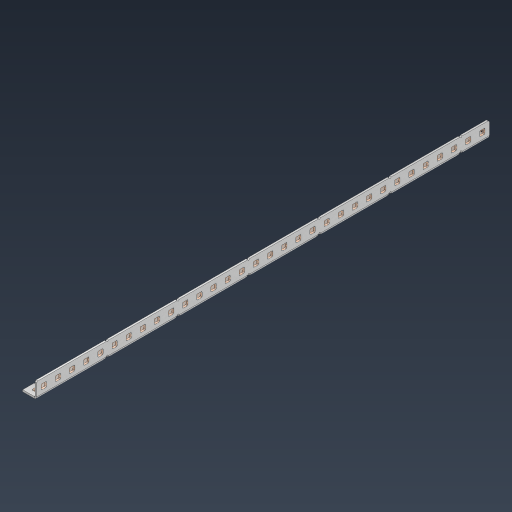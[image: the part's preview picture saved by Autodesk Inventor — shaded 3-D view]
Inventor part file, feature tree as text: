
AUTODESK INVENTOR PART (.ipt)
format: ipt  version: 2024.3 (Build 283343000, 343)  size: 1,180,160 bytes
history: native  units: in
note: dims shown in document units (in); Inventor stores cm internally (conversion verified against a paired STEP export)
features: other x103, extrude x94, sheet_metal_op x11, pattern_linear x2, mirror x1, chamfer x1, sketch x1
ambient origin geometry x8: Origin, YZ Plane, XZ Plane, XY Plane, X Axis, Y Axis, Z Axis, Center Point
bodies: Solid1 (feature_tree), Body (feature_tree)
feature tree (213):
  sheet_metal_op  "Flanges"
  other  "Flange Pattern Plane"
  other  "Flange Pattern Sketch"
  sheet_metal_op  "Flange Pattern"
  sheet_metal_op  "Body Pattern"
  pattern_linear  "Center Pattern"  Spacing1=16.0in  [1 undecoded]
  other  "Arc Length"
  mirror  "Notch Mirror"
  pattern_linear  "Notch Pattern"  Spacing1=0.0625in  [1 undecoded]
  chamfer  "End Chamfer"
  extrude  "Half Cut"  Depth=0.0625in
  other  "Plate1"
  sketch  "Sketch2"  dims[d0=1.0in d1=16.0in d2=0.0625in d3=0.0625in d4=0.0312in d5=0.125in d6=0.0625in d7=0.5in d8=90.0deg d9=0.0312in d10=0.25in d11=0.0625in d12=0.0625in d16=0.182in d17=0.02in d18=0.0625in d19=0.0in d20=0.25in d21=0.25in d38=12.5984in d40=0.5in d41=0.3937in d43=1.0in d46=0.172in d47=1.0in d48=0.0in d49=0.182in d50=0.02in d51=0.25in d52=0.25in d53=0.0625in d54=0.0in d55=0.172in d56=1.0in d57=0.0in d58=0.25in d60=12.5984in d62=0.5in d63=0.3937in d65=0.5in d85=0.1473in d86=0.1782in d88=0.04in d89=0.0625in d90=0.0in d91=0.04in d92=0.0491in d95=2.5in d96=0.04in d97=0.25in d98=45.0deg d99=0.25in d100=0.5in d101=0.0in d102=2.497in d106=0.182in d107=0.02in d108=0.5in d109=0.5in d110=0.0625in d111=0.0in d112=0.172in d113=0.5in d114=0.0in d117=0.5in d118=0.5in d119=0.5in]
  other  "Plate2"
  sheet_metal_op  "Bend1"
  sheet_metal_op  "Corner1"
  other  "Srf1"
  other  "Srf2"
  other  "Srf91"
  sheet_metal_op  "Body Pattern Sketch"
  other  "Srf92"
  other  "Srf786"
  other  "Srf823"
  other  "Srf824"
  other  "Srf825"
  other  "Srf826"
  other  "Srf827"
  other  "Srf828"
  other  "Srf829"
  other  "Srf856"
  other  "Srf857"
  other  "Srf858"
  other  "Srf859"
  other  "Srf860"
  other  "Srf861"
  other  "Srf862"
  other  "Srf889"
  other  "Srf890"
  other  "Srf891"
  other  "Srf892"
  other  "Srf893"
  other  "Srf894"
  other  "Srf895"
  other  "Srf896"
  other  "Srf922"
  other  "Srf923"
  other  "Srf924"
  other  "Srf925"
  other  "Srf926"
  other  "Srf959"
  other  "Srf960"
  other  "Srf961"
  other  "Srf962"
  other  "Srf963"
  other  "Srf996"
  other  "Srf997"
  other  "Srf998"
  other  "Srf999"
  other  "Srf1000"
  other  "Srf1143"
  other  "Srf1144"
  other  "Srf1145"
  other  "Srf1146"
  other  "Srf1147"
  other  "Srf1148"
  other  "Srf1149"
  other  "Srf1150"
  other  "Srf1151"
  other  "Srf1152"
  other  "Srf1153"
  other  "Srf1154"
  other  "Srf1155"
  other  "Srf1156"
  other  "Srf1157"
  other  "Srf1158"
  other  "Srf1159"
  other  "Srf1160"
  other  "Srf1199"
  other  "Srf1200"
  other  "Srf1201"
  other  "Srf1202"
  other  "Srf1203"
  other  "Srf1204"
  other  "Srf1205"
  other  "Srf1206"
  other  "Srf1207"
  other  "Srf1208"
  other  "Srf1209"
  other  "Srf1210"
  other  "Srf1211"
  other  "Srf1212"
  other  "Srf1213"
  other  "Srf1214"
  other  "Srf1215"
  other  "Srf1216"
  other  "Srf1255"
  other  "Srf1256"
  other  "Srf1257"
  other  "Srf1258"
  other  "Srf1259"
  other  "Srf1260"
  other  "Srf1261"
  other  "Srf1262"
  other  "Srf1263"
  other  "Srf1264"
  other  "Srf1265"
  other  "Srf1266"
  other  "Srf1267"
  other  "Srf1268"
  other  "Srf1269"
  other  "Srf1270"
  other  "Srf1271"
  other  "Srf1272"
  sheet_metal_op  "Flange Stamp"
  sheet_metal_op  "Flange Circle"
  sheet_metal_op  "Body Stamp"
  sheet_metal_op  "Body Circle"
  other  "Center Stamp"
  other  "Center Circle"
  sheet_metal_op  "Notch"
  extrude  "ExtrusionSrf2"  Depth=0.0312in
  extrude  "ExtrusionSrf92"  Depth=0.5in
  extrude  "ExtrusionSrf823"  Depth=0.0625in
  extrude  "ExtrusionSrf824"  Depth=0.5in TaperAngle=90.0deg
  extrude  "ExtrusionSrf825"  Depth=0.25in
  extrude  "ExtrusionSrf826"  Depth=0.0625in
  extrude  "ExtrusionSrf827"  Depth=0.0625in
  extrude  "ExtrusionSrf828"  Depth=0.182in
  extrude  "ExtrusionSrf829"  Depth=0.02in
  extrude  "ExtrusionSrf856"  Depth=0.0625in
  extrude  "ExtrusionSrf857"  TaperAngle=0.0deg  [1 undecoded]
  extrude  "ExtrusionSrf858"  Depth=0.25in
  extrude  "ExtrusionSrf859"  Depth=0.25in
  extrude  "ExtrusionSrf860"  Depth=0.5in
  extrude  "ExtrusionSrf861"  Depth=0.5in
  extrude  "ExtrusionSrf862"  Depth=1.0in TaperAngle=0.0deg
  extrude  "ExtrusionSrf889"  Depth=0.182in
  extrude  "ExtrusionSrf890"  Depth=0.02in
  extrude  "ExtrusionSrf891"  Depth=0.25in
  extrude  "ExtrusionSrf892"  Depth=0.25in
  extrude  "ExtrusionSrf893"  Depth=0.0625in
  extrude  "ExtrusionSrf894"  TaperAngle=0.0deg  [1 undecoded]
  extrude  "ExtrusionSrf895"  Depth=0.5in
  extrude  "ExtrusionSrf896"  Depth=1.0in TaperAngle=0.0deg
  extrude  "ExtrusionSrf922"  Depth=0.25in
  extrude  "ExtrusionSrf923"  Depth=0.5in
  extrude  "ExtrusionSrf924"  Depth=0.5in
  extrude  "ExtrusionSrf925"  Depth=0.5in
  extrude  "ExtrusionSrf926"  Depth=0.5in
  extrude  "ExtrusionSrf959"  Depth=0.5in
  extrude  "ExtrusionSrf960"  Depth=0.0625in
  extrude  "ExtrusionSrf961"  TaperAngle=0.0deg  [1 undecoded]
  extrude  "ExtrusionSrf962"  Depth=0.5in
  extrude  "ExtrusionSrf963"  Depth=0.5in
  extrude  "ExtrusionSrf996"  Depth=2.5in
  extrude  "ExtrusionSrf997"  Depth=0.25in TaperAngle=45.0deg
  extrude  "ExtrusionSrf998"  Depth=0.25in
  extrude  "ExtrusionSrf999"  Depth=0.5in TaperAngle=0.0deg
  extrude  "ExtrusionSrf1000"  Depth=0.5in
  extrude  "ExtrusionSrf1143"  Depth=0.182in
  extrude  "ExtrusionSrf1144"  Depth=0.02in
  extrude  "ExtrusionSrf1145"  Depth=0.5in
  extrude  "ExtrusionSrf1146"  Depth=0.5in
  extrude  "ExtrusionSrf1147"  Depth=0.0625in
  extrude  "ExtrusionSrf1148"  TaperAngle=0.0deg  [1 undecoded]
  extrude  "ExtrusionSrf1149"  Depth=0.5in
  extrude  "ExtrusionSrf1150"  Depth=0.5in TaperAngle=0.0deg
  extrude  "ExtrusionSrf1151"  Depth=0.5in
  extrude  "ExtrusionSrf1152"  Depth=0.5in
  extrude  "ExtrusionSrf1153"  Depth=0.5in
  extrude  "ExtrusionSrf1154"  [1 undecoded]
  extrude  "ExtrusionSrf1155"  [1 undecoded]
  extrude  "ExtrusionSrf1156"  [1 undecoded]
  extrude  "ExtrusionSrf1157"  [1 undecoded]
  extrude  "ExtrusionSrf1158"  [1 undecoded]
  extrude  "ExtrusionSrf1159"  [1 undecoded]
  extrude  "ExtrusionSrf1160"  [1 undecoded]
  extrude  "ExtrusionSrf1199"  [1 undecoded]
  extrude  "ExtrusionSrf1200"  [1 undecoded]
  extrude  "ExtrusionSrf1201"  [1 undecoded]
  extrude  "ExtrusionSrf1202"  [1 undecoded]
  extrude  "ExtrusionSrf1203"  [1 undecoded]
  extrude  "ExtrusionSrf1204"  [1 undecoded]
  extrude  "ExtrusionSrf1205"  [1 undecoded]
  extrude  "ExtrusionSrf1206"  [1 undecoded]
  extrude  "ExtrusionSrf1207"  [1 undecoded]
  extrude  "ExtrusionSrf1208"  [1 undecoded]
  extrude  "ExtrusionSrf1209"  [1 undecoded]
  extrude  "ExtrusionSrf1210"  [1 undecoded]
  extrude  "ExtrusionSrf1211"  [1 undecoded]
  extrude  "ExtrusionSrf1212"  [1 undecoded]
  extrude  "ExtrusionSrf1213"  [1 undecoded]
  extrude  "ExtrusionSrf1214"  [1 undecoded]
  extrude  "ExtrusionSrf1215"  [1 undecoded]
  extrude  "ExtrusionSrf1216"  [1 undecoded]
  extrude  "ExtrusionSrf1255"  [1 undecoded]
  extrude  "ExtrusionSrf1256"  [1 undecoded]
  extrude  "ExtrusionSrf1257"  [1 undecoded]
  extrude  "ExtrusionSrf1258"  [1 undecoded]
  extrude  "ExtrusionSrf1259"  [1 undecoded]
  extrude  "ExtrusionSrf1260"  [1 undecoded]
  extrude  "ExtrusionSrf1261"  [1 undecoded]
  extrude  "ExtrusionSrf1262"  [1 undecoded]
  extrude  "ExtrusionSrf1263"  [1 undecoded]
  extrude  "ExtrusionSrf1264"  [1 undecoded]
  extrude  "ExtrusionSrf1265"  [1 undecoded]
  extrude  "ExtrusionSrf1266"  [1 undecoded]
  extrude  "ExtrusionSrf1267"  [1 undecoded]
  extrude  "ExtrusionSrf1268"  [1 undecoded]
  extrude  "ExtrusionSrf1269"  [1 undecoded]
  extrude  "ExtrusionSrf1270"  [1 undecoded]
  extrude  "ExtrusionSrf1271"  [1 undecoded]
  extrude  "ExtrusionSrf1272"  [1 undecoded]
note: 49 required parameter values undecoded (feature->parameter linkage not recoverable at this tier; creation-order binding heuristic only, values carry confidence <= 0.55)
